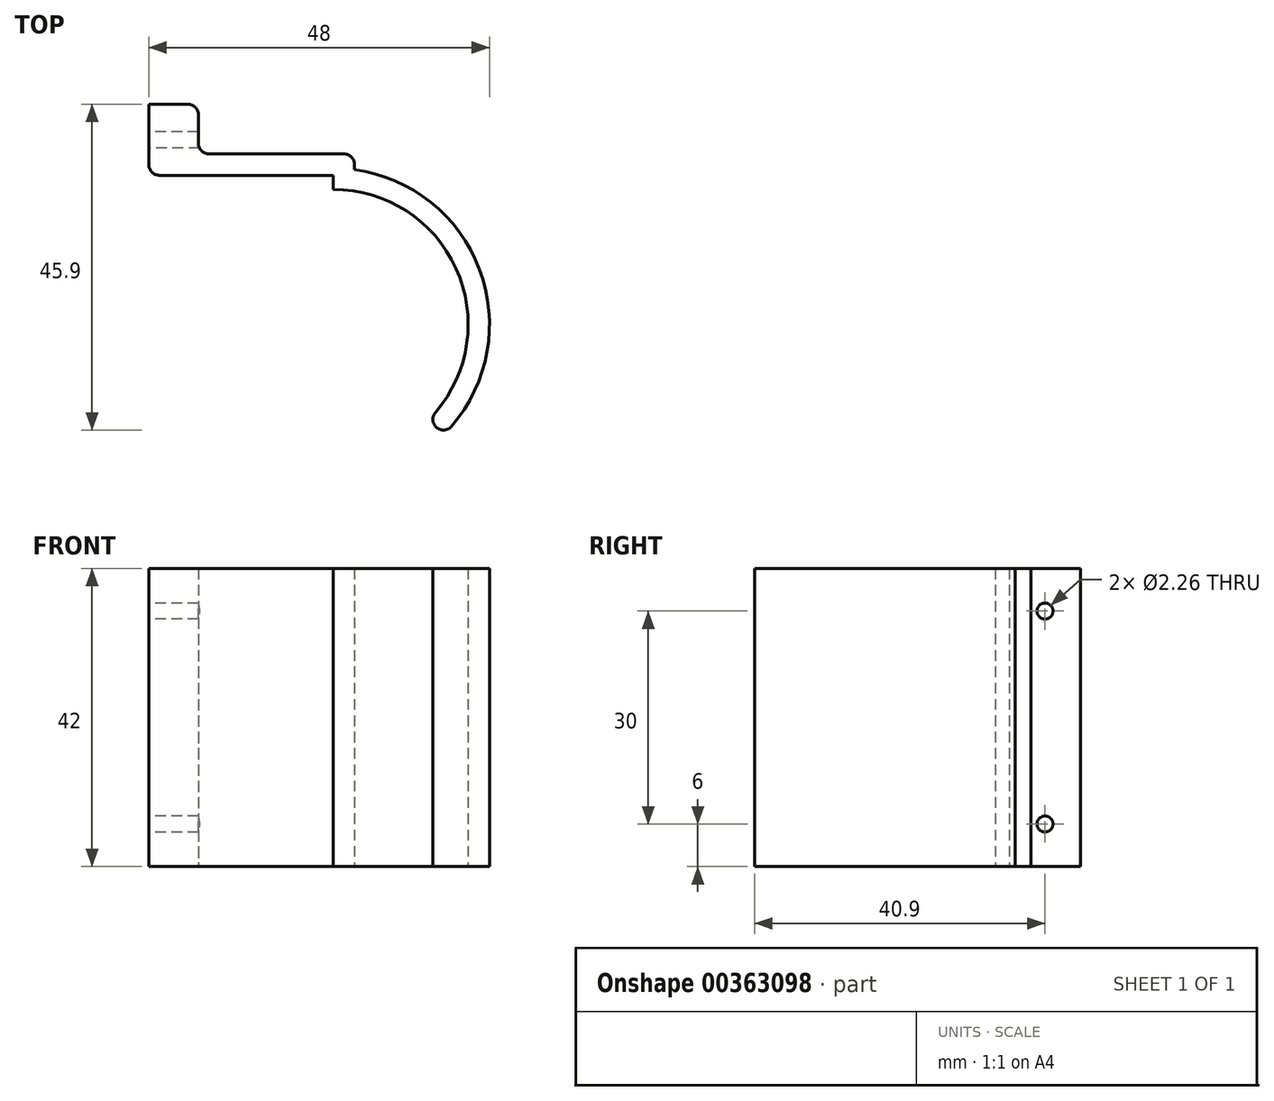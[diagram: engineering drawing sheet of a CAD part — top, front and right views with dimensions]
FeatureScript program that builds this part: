
annotation { "Feature Type Name" : "Feature", "Feature Type Description" : "" }
export const myFeature = defineFeature(function(context is Context, id is Id, definition is map)
    precondition{}
    {
        {
            var Q0;
            Q0=qCreatedBy(makeId("Top.planeOp"),FACE);
            var sketch = newSketch(context, id + "F0", { "sketchPlane" : qUnion([Q0])});
            skArc(sketch, "E0", {"start": v(13.44, -13.44) * mm, "mid": v(17.55, 7.27) * mm, "end": v(0, 19) * mm});
            skLineSegment(sketch, "E1", {"start": v(0, 19) * mm, "end": v(0, 21) * mm});
            skLineSegment(sketch, "E2", {"start": v(0, 21) * mm, "end": v(-26, 21) * mm});
            skLineSegment(sketch, "E3", {"start": v(-26, 21) * mm, "end": v(-26, 31) * mm});
            skLineSegment(sketch, "E4", {"start": v(-26, 31) * mm, "end": v(-19, 31) * mm});
            skLineSegment(sketch, "E5", {"start": v(-19, 31) * mm, "end": v(-19, 24) * mm});
            skLineSegment(sketch, "E6", {"start": v(-19, 24) * mm, "end": v(3, 24) * mm});
            skArc(sketch, "E7", {"start": v(15.56, -15.56) * mm, "mid": v(20.85, 7.01) * mm, "end": v(3, 21.8) * mm});
            skLineSegment(sketch, "E8", {"start": v(3, 24) * mm, "end": v(3, 21.8) * mm});
            skLineSegment(sketch, "E9", {"start": v(13.44, -13.44) * mm, "end": v(15.56, -15.56) * mm});
            skSolve(sketch);
        }
        {
            var Q0;
            Q0 = qSketchRegion(id + "F0", true);
            extrude(context, id + "F1", {"entities" : qUnion([Q0]), "depth" : 42 * mm});
        }
        {
            var Q0;
            Q0=makeQuery(id+"F1.opExtrude","SWEPT_EDGE",EDGE,{"disambiguationData":[OSD([sQuery(id+"F0.wireOp",EDGE,"E0"),sQuery(id+"F0.wireOp",EDGE,"E9")])]});
            var Q1;
            Q1=makeQuery(id+"F1.opExtrude","SWEPT_EDGE",EDGE,{"disambiguationData":[OSD([sQuery(id+"F0.wireOp",EDGE,"E7"),sQuery(id+"F0.wireOp",EDGE,"E9")])]});
            var Q2;
            Q2=makeQuery(id+"F1.opExtrude","SWEPT_EDGE",EDGE,{"disambiguationData":[OSD([sQuery(id+"F0.wireOp",EDGE,"E2"),sQuery(id+"F0.wireOp",EDGE,"E3")])]});
            var Q3;
            Q3=makeQuery(id+"F1.opExtrude","SWEPT_EDGE",EDGE,{"disambiguationData":[OSD([sQuery(id+"F0.wireOp",EDGE,"E6"),sQuery(id+"F0.wireOp",EDGE,"E8")])]});
            var Q4;
            Q4=makeQuery(id+"F1.opExtrude","SWEPT_EDGE",EDGE,{"disambiguationData":[OSD([sQuery(id+"F0.wireOp",EDGE,"E5"),sQuery(id+"F0.wireOp",EDGE,"E6")])]});
            var Q5;
            Q5=makeQuery(id+"F1.opExtrude","SWEPT_EDGE",EDGE,{"disambiguationData":[OSD([sQuery(id+"F0.wireOp",EDGE,"E4"),sQuery(id+"F0.wireOp",EDGE,"E5")])]});
            fillet(context, id + "F2", {"entities" : qUnion([Q0, Q1, Q2, Q3, Q4, Q5]), "radius" : 1.5 * mm, "tangentPropagation" : true, "allowEdgeOverflow" : false});
        }
        {
            var Q0;
            Q0=makeQuery(id+"F1.opExtrude","SWEPT_FACE",FACE,{"disambiguationData":[OSD([sQuery(id+"F0.wireOp",EDGE,"E3")])]});
            var sketch = newSketch(context, id + "F3", { "sketchPlane" : qUnion([Q0])});
            skPoint(sketch, "E10", {"position": v(-26, 36) * mm});
            skPoint(sketch, "E11", {"position": v(-26, 6) * mm});
            skSolve(sketch);
        }
        {
            var Q0;
            Q0=sQuery(id+"F3.wireOp",VERTEX,"E10");
            var Q1;
            Q1=sQuery(id+"F3.wireOp",VERTEX,"E11");
            var Q2;
            Q2=makeQuery(id+"F1.opExtrude","SWEPT_BODY",BODY,{"disambiguationData":[OSD([sQuery(id+"F0.wireOp",EDGE,"E0"),sQuery(id+"F0.wireOp",EDGE,"E1"),sQuery(id+"F0.wireOp",EDGE,"E2"),sQuery(id+"F0.wireOp",EDGE,"E3"),sQuery(id+"F0.wireOp",EDGE,"E4"),sQuery(id+"F0.wireOp",EDGE,"E5"),sQuery(id+"F0.wireOp",EDGE,"E6"),sQuery(id+"F0.wireOp",EDGE,"E7"),sQuery(id+"F0.wireOp",EDGE,"E8"),sQuery(id+"F0.wireOp",EDGE,"E9")])]});
            hole(context, id + "F4", {"style" : HoleStyle.SIMPLE, "endStyle" : HoleEndStyle.BLIND, "standardTappedOrClearance" : lookupTablePath({ "standard" : "ANSI", "engagement" : "75%", "pitch" : "40 tpi", "size" : "#4", "type" : "Tapped" }), "standardBlindInLast" : lookupTablePath({ "standard" : "ANSI", "engagement" : "75%", "pitch" : "40 tpi", "size" : "#4", "type" : "Tapped" }), "holeDiameter" : 2.26 * mm, "showTappedDepth" : true, "holeDepth" : 18.57 * mm, "isTappedThrough" : true, "tappedDepth" : 16.67 * mm, "tapClearance" : 3, "locations" : qUnion([Q0, Q1]), "scope" : qUnion([Q2]), "majorDiameter" : 2.84 * mm});
        }
    });
